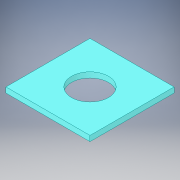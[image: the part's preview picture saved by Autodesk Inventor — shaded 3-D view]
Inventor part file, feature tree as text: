
AUTODESK INVENTOR PART (.ipt)
format: ipt  version: 2019 (Build 230136000, 136)  size: 112,640 bytes
history: native  units: mm
features: extrude x1, sketch x1
ambient origin geometry x8: Origin, YZ Plane, XZ Plane, XY Plane, X Axis, Y Axis, Z Axis, Center Point
bodies: Solid1 (feature_tree)
feature tree (2):
  extrude  "Extrusion1"  Depth=50.0mm
  sketch  "Sketch1"  dims[d0=50.0mm d1=50.0mm d2=22.0mm d3=3.18mm d4=0.0mm]
